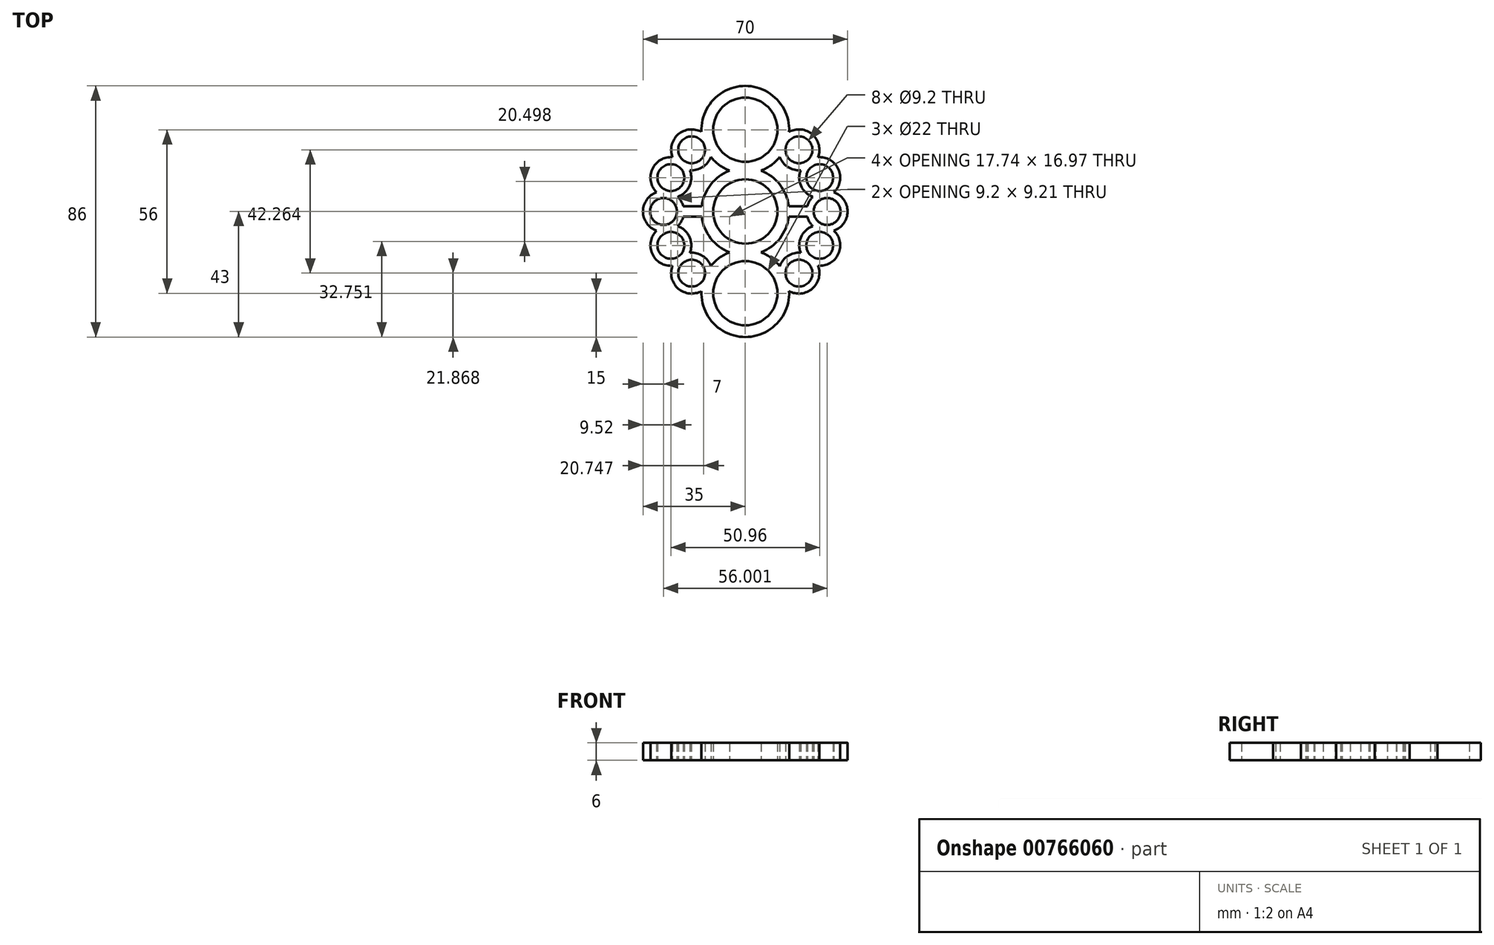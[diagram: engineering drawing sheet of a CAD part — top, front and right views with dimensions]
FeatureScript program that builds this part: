
annotation { "Feature Type Name" : "Feature", "Feature Type Description" : "" }
export const myFeature = defineFeature(function(context is Context, id is Id, definition is map)
    precondition{}
    {
        {
            var Q0;
            Q0=qCreatedBy(makeId("Top.planeOp"),FACE);
            var sketch = newSketch(context, id + "F0", { "sketchPlane" : qUnion([Q0])});
            skArc(sketch, "E0", {"start": v(11, 0) * mm, "mid": v(7.78, 7.78) * mm, "end": v(0, 11) * mm});
            skArc(sketch, "E1", {"start": v(14.9, 1.77) * mm, "mid": v(11.84, 9.2) * mm, "end": v(5.39, 14) * mm});
            skArc(sketch, "E2", {"start": v(0, 17) * mm, "mid": v(11, 28) * mm, "end": v(0, 39) * mm});
            skArc(sketch, "E3", {"start": v(14.98, 27.14) * mm, "mid": v(10.9, 38.3) * mm, "end": v(0, 43) * mm});
            skArc(sketch, "E4", {"start": v(14.98, 27.14) * mm, "mid": v(14.93, 27.17) * mm, "end": v(14.88, 27.2) * mm});
            skArc(sketch, "E5", {"start": v(13.85, 22) * mm, "mid": v(13.81, 22.03) * mm, "end": v(13.77, 22.05) * mm});
            skArc(sketch, "E6", {"start": v(32.6, 0) * mm, "mid": v(28, 4.6) * mm, "end": v(23.4, 0) * mm});
            skArc(sketch, "E7", {"start": v(23.12, 5.02) * mm, "mid": v(21.95, 3.52) * mm, "end": v(21.23, 1.77) * mm});
            skCircle(sketch, "E8", {"center": v(18.37, 21.13) * mm, "radius": 4.6 * mm});
            skArc(sketch, "E9", {"start": v(24.86, 18.52) * mm, "mid": v(22.96, 26.41) * mm, "end": v(14.88, 27.2) * mm});
            skCircle(sketch, "E10", {"center": v(25.48, 11.61) * mm, "radius": 4.6 * mm});
            skArc(sketch, "E11", {"start": v(30.3, 6.54) * mm, "mid": v(31.85, 14.52) * mm, "end": v(24.82, 18.58) * mm});
            skArc(sketch, "E12.trimOffspring", {"start": v(24.86, 18.52) * mm, "mid": v(24.84, 18.55) * mm, "end": v(24.82, 18.58) * mm});
            skArc(sketch, "E13.trimOffspring", {"start": v(30.3, 6.54) * mm, "mid": v(30.3, 6.58) * mm, "end": v(30.29, 6.62) * mm});
            skArc(sketch, "E14.trimOffspring", {"start": v(18.96, 14.16) * mm, "mid": v(19.11, 8.71) * mm, "end": v(23.12, 5.02) * mm});
            skArc(sketch, "E15.trimOffspring", {"start": v(11.8, 18.73) * mm, "mid": v(14.6, 15.23) * mm, "end": v(18.96, 14.16) * mm});
            skArc(sketch, "E16.trimOffspring", {"start": v(5.39, 14) * mm, "mid": v(8.9, 15.93) * mm, "end": v(11.8, 18.73) * mm});
            skArc(sketch, "E17.trimOffspring", {"start": v(35, 0) * mm, "mid": v(33.7, 4.06) * mm, "end": v(30.29, 6.62) * mm});
            skLineSegment(sketch, "E18", {"start": v(14.9, 1.77) * mm, "end": v(21.23, 1.77) * mm});
            skArc(sketch, "E19.MirrorCS", {"start": v(-24.86, 18.52) * mm, "mid": v(-24.84, 18.55) * mm, "end": v(-24.82, 18.58) * mm});
            skArc(sketch, "E20.MirrorCS", {"start": v(-13.85, 22) * mm, "mid": v(-13.81, 22.03) * mm, "end": v(-13.77, 22.05) * mm});
            skArc(sketch, "E21.MirrorCS", {"start": v(-14.98, 27.14) * mm, "mid": v(-14.93, 27.17) * mm, "end": v(-14.88, 27.2) * mm});
            skArc(sketch, "E22.MirrorCS", {"start": v(-30.3, 6.54) * mm, "mid": v(-30.3, 6.58) * mm, "end": v(-30.29, 6.62) * mm});
            skArc(sketch, "E23.MirrorCS", {"start": v(-5.39, 14) * mm, "mid": v(-8.9, 15.93) * mm, "end": v(-11.8, 18.73) * mm});
            skArc(sketch, "E24.MirrorCS", {"start": v(-14.9, 1.77) * mm, "mid": v(-11.84, 9.2) * mm, "end": v(-5.39, 14) * mm});
            skArc(sketch, "E25.MirrorCS", {"start": v(-32.6, 0) * mm, "mid": v(-28, 4.6) * mm, "end": v(-23.4, 0) * mm});
            skCircle(sketch, "E26.MirrorC", {"center": v(-25.48, 11.61) * mm, "radius": 4.6 * mm});
            skArc(sketch, "E27.MirrorCS", {"start": v(-14.98, 27.14) * mm, "mid": v(-10.9, 38.3) * mm, "end": v(0, 43) * mm});
            skLineSegment(sketch, "E28.MirrorCS", {"start": v(-14.9, 1.77) * mm, "end": v(-21.23, 1.77) * mm});
            skArc(sketch, "E29.MirrorCS", {"start": v(-18.96, 14.16) * mm, "mid": v(-19.11, 8.71) * mm, "end": v(-23.12, 5.02) * mm});
            skArc(sketch, "E30.MirrorCS", {"start": v(-35, 0) * mm, "mid": v(-33.7, 4.06) * mm, "end": v(-30.29, 6.62) * mm});
            skCircle(sketch, "E31.MirrorC", {"center": v(-18.37, 21.13) * mm, "radius": 4.6 * mm});
            skArc(sketch, "E32.MirrorCS", {"start": v(-30.3, 6.54) * mm, "mid": v(-31.85, 14.52) * mm, "end": v(-24.82, 18.58) * mm});
            skArc(sketch, "E33.MirrorCS", {"start": v(-11, 0) * mm, "mid": v(-7.78, 7.78) * mm, "end": v(0, 11) * mm});
            skArc(sketch, "E34.MirrorCS", {"start": v(-23.12, 5.02) * mm, "mid": v(-21.95, 3.52) * mm, "end": v(-21.23, 1.77) * mm});
            skArc(sketch, "E35.MirrorCS", {"start": v(-24.86, 18.52) * mm, "mid": v(-22.96, 26.41) * mm, "end": v(-14.88, 27.2) * mm});
            skArc(sketch, "E36.MirrorCS", {"start": v(-11.8, 18.73) * mm, "mid": v(-14.6, 15.23) * mm, "end": v(-18.96, 14.16) * mm});
            skArc(sketch, "E37.MirrorCS", {"start": v(0, 17) * mm, "mid": v(-11, 28) * mm, "end": v(0, 39) * mm});
            skArc(sketch, "E38.MirrorCS", {"start": v(14.98, -27.14) * mm, "mid": v(14.93, -27.17) * mm, "end": v(14.88, -27.2) * mm});
            skArc(sketch, "E39.MirrorCS", {"start": v(-30.3, -6.54) * mm, "mid": v(-30.3, -6.58) * mm, "end": v(-30.29, -6.62) * mm});
            skArc(sketch, "E40.MirrorCS", {"start": v(-14.98, -27.14) * mm, "mid": v(-14.93, -27.17) * mm, "end": v(-14.88, -27.2) * mm});
            skArc(sketch, "E41.MirrorCS", {"start": v(30.3, -6.54) * mm, "mid": v(30.3, -6.58) * mm, "end": v(30.29, -6.62) * mm});
            skArc(sketch, "E42.MirrorCS", {"start": v(13.85, -22) * mm, "mid": v(13.81, -22.03) * mm, "end": v(13.77, -22.05) * mm});
            skArc(sketch, "E43.MirrorCS", {"start": v(-13.85, -22) * mm, "mid": v(-13.81, -22.03) * mm, "end": v(-13.77, -22.05) * mm});
            skArc(sketch, "E44.MirrorCS", {"start": v(24.86, -18.52) * mm, "mid": v(24.84, -18.55) * mm, "end": v(24.82, -18.58) * mm});
            skArc(sketch, "E45.MirrorCS", {"start": v(-24.86, -18.52) * mm, "mid": v(-24.84, -18.55) * mm, "end": v(-24.82, -18.58) * mm});
            skArc(sketch, "E46.MirrorCS", {"start": v(35, 0) * mm, "mid": v(33.7, -4.06) * mm, "end": v(30.29, -6.62) * mm});
            skArc(sketch, "E47.MirrorCS", {"start": v(32.6, 0) * mm, "mid": v(28, -4.6) * mm, "end": v(23.4, 0) * mm});
            skArc(sketch, "E48.MirrorCS", {"start": v(-18.96, -14.16) * mm, "mid": v(-19.11, -8.71) * mm, "end": v(-23.12, -5.02) * mm});
            skCircle(sketch, "E49.MirrorC", {"center": v(25.48, -11.61) * mm, "radius": 4.6 * mm});
            skArc(sketch, "E50.MirrorCS", {"start": v(18.96, -14.16) * mm, "mid": v(19.11, -8.71) * mm, "end": v(23.12, -5.02) * mm});
            skArc(sketch, "E51.MirrorCS", {"start": v(30.3, -6.54) * mm, "mid": v(31.85, -14.52) * mm, "end": v(24.82, -18.58) * mm});
            skCircle(sketch, "E52.MirrorC", {"center": v(18.37, -21.13) * mm, "radius": 4.6 * mm});
            skArc(sketch, "E53.MirrorCS", {"start": v(11.8, -18.73) * mm, "mid": v(14.6, -15.23) * mm, "end": v(18.96, -14.16) * mm});
            skArc(sketch, "E54.MirrorCS", {"start": v(5.39, -14) * mm, "mid": v(8.9, -15.93) * mm, "end": v(11.8, -18.73) * mm});
            skArc(sketch, "E55.MirrorCS", {"start": v(24.86, -18.52) * mm, "mid": v(22.96, -26.41) * mm, "end": v(14.88, -27.2) * mm});
            skArc(sketch, "E56.MirrorCS", {"start": v(-32.6, 0) * mm, "mid": v(-28, -4.6) * mm, "end": v(-23.4, 0) * mm});
            skLineSegment(sketch, "E57.MirrorCS", {"start": v(14.9, -1.77) * mm, "end": v(21.23, -1.77) * mm});
            skArc(sketch, "E58.MirrorCS", {"start": v(-11.8, -18.73) * mm, "mid": v(-14.6, -15.23) * mm, "end": v(-18.96, -14.16) * mm});
            skArc(sketch, "E59.MirrorCS", {"start": v(-5.39, -14) * mm, "mid": v(-8.9, -15.93) * mm, "end": v(-11.8, -18.73) * mm});
            skArc(sketch, "E60.MirrorCS", {"start": v(11, 0) * mm, "mid": v(7.78, -7.78) * mm, "end": v(0, -11) * mm});
            skArc(sketch, "E61.MirrorCS", {"start": v(-11, 0) * mm, "mid": v(-7.78, -7.78) * mm, "end": v(0, -11) * mm});
            skArc(sketch, "E62.MirrorCS", {"start": v(-35, 0) * mm, "mid": v(-33.7, -4.06) * mm, "end": v(-30.29, -6.62) * mm});
            skArc(sketch, "E63.MirrorCS", {"start": v(0, -17) * mm, "mid": v(11, -28) * mm, "end": v(0, -39) * mm});
            skArc(sketch, "E64.MirrorCS", {"start": v(-30.3, -6.54) * mm, "mid": v(-31.85, -14.52) * mm, "end": v(-24.82, -18.58) * mm});
            skCircle(sketch, "E65.MirrorC", {"center": v(-25.48, -11.61) * mm, "radius": 4.6 * mm});
            skCircle(sketch, "E66.MirrorC", {"center": v(-18.37, -21.13) * mm, "radius": 4.6 * mm});
            skLineSegment(sketch, "E67.MirrorCS", {"start": v(-14.9, -1.77) * mm, "end": v(-21.23, -1.77) * mm});
            skArc(sketch, "E68.MirrorCS", {"start": v(14.9, -1.77) * mm, "mid": v(11.84, -9.2) * mm, "end": v(5.39, -14) * mm});
            skArc(sketch, "E69.MirrorCS", {"start": v(0, -17) * mm, "mid": v(-11, -28) * mm, "end": v(0, -39) * mm});
            skArc(sketch, "E70.MirrorCS", {"start": v(-14.9, -1.77) * mm, "mid": v(-11.84, -9.2) * mm, "end": v(-5.39, -14) * mm});
            skArc(sketch, "E71.MirrorCS", {"start": v(23.12, -5.02) * mm, "mid": v(21.95, -3.52) * mm, "end": v(21.23, -1.77) * mm});
            skArc(sketch, "E72.MirrorCS", {"start": v(-24.86, -18.52) * mm, "mid": v(-22.96, -26.41) * mm, "end": v(-14.88, -27.2) * mm});
            skArc(sketch, "E73.MirrorCS", {"start": v(-23.12, -5.02) * mm, "mid": v(-21.95, -3.52) * mm, "end": v(-21.23, -1.77) * mm});
            skArc(sketch, "E74.MirrorCS", {"start": v(14.98, -27.14) * mm, "mid": v(10.9, -38.3) * mm, "end": v(0, -43) * mm});
            skArc(sketch, "E75.MirrorCS", {"start": v(-14.98, -27.14) * mm, "mid": v(-10.9, -38.3) * mm, "end": v(0, -43) * mm});
            skSolve(sketch);
        }
        {
            var Q0;
            Q0 = qSketchRegion(id + "F0", true);
            extrude(context, id + "F1", {"entities" : qUnion([Q0]), "depth" : 6 * mm, "offsetDistance" : 25 * mm});
        }
    });
